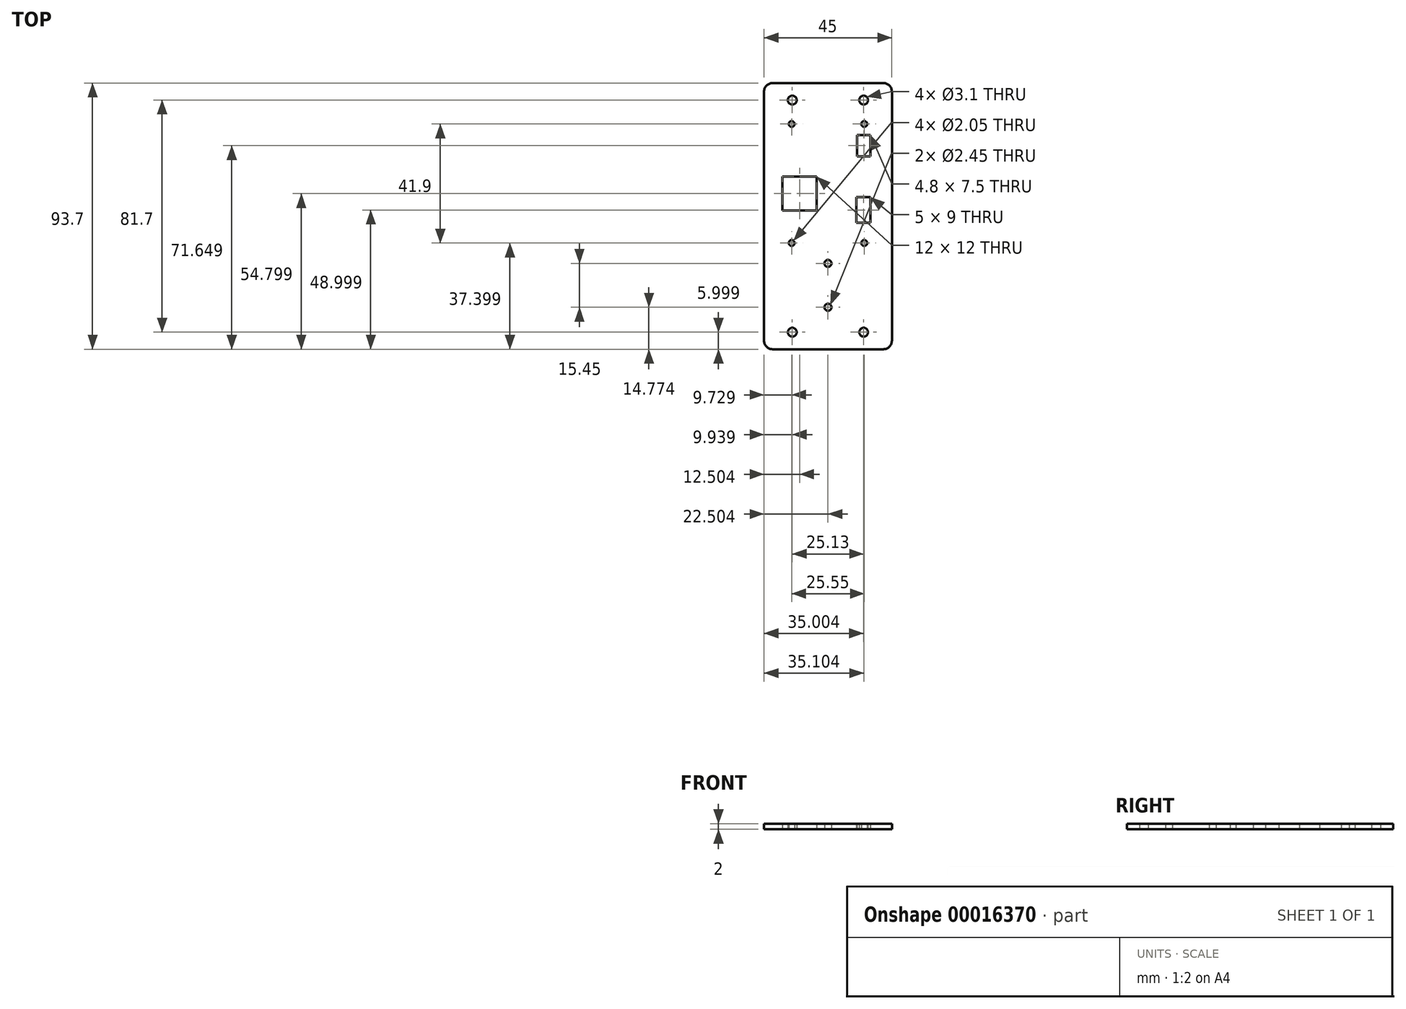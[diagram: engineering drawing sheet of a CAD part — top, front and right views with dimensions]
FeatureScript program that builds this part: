
annotation { "Feature Type Name" : "Feature", "Feature Type Description" : "" }
export const myFeature = defineFeature(function(context is Context, id is Id, definition is map)
    precondition{}
    {
        {
            var Q0;
            Q0=qCreatedBy(makeId("Top.planeOp"),FACE);
            var sketch = newSketch(context, id + "F0", { "sketchPlane" : qUnion([Q0])});
            skLineSegment(sketch, "E0.bottom", {"start": v(-24.75, 105.77) * mm, "end": v(14.25, 105.77) * mm});
            skLineSegment(sketch, "E0.top", {"start": v(-24.75, 12.07) * mm, "end": v(14.25, 12.07) * mm});
            skLineSegment(sketch, "E0.left", {"start": v(-27.75, 102.77) * mm, "end": v(-27.75, 15.07) * mm});
            skLineSegment(sketch, "E0.right", {"start": v(17.25, 102.77) * mm, "end": v(17.25, 15.07) * mm});
            skLineSegment(sketch, "E1.bottom", {"start": v(-20.25, 93.77) * mm, "end": v(9.75, 93.77) * mm});
            skLineSegment(sketch, "E1.top", {"start": v(-20.25, 47.07) * mm, "end": v(9.75, 47.07) * mm});
            skLineSegment(sketch, "E1.left", {"start": v(-20.25, 93.77) * mm, "end": v(-20.25, 47.07) * mm});
            skLineSegment(sketch, "E1.right", {"start": v(9.75, 93.77) * mm, "end": v(9.75, 47.07) * mm});
            skPoint(sketch, "E2", {"position": v(-5.25, 105.77) * mm});
            skPoint(sketch, "E3", {"position": v(-5.25, 93.77) * mm});
            skLineSegment(sketch, "E4.bottom", {"start": v(-20.25, 103.77) * mm, "end": v(9.75, 103.77) * mm});
            skLineSegment(sketch, "E4.top", {"start": v(-20.25, 95.77) * mm, "end": v(9.75, 95.77) * mm});
            skLineSegment(sketch, "E4.left", {"start": v(-20.25, 103.77) * mm, "end": v(-20.25, 95.77) * mm});
            skLineSegment(sketch, "E4.right", {"start": v(9.75, 103.77) * mm, "end": v(9.75, 95.77) * mm});
            skPoint(sketch, "E5", {"position": v(-5.25, 103.77) * mm});
            skCircle(sketch, "E6", {"center": v(-17.81, 99.77) * mm, "radius": 1.55 * mm});
            skCircle(sketch, "E7", {"center": v(7.32, 99.77) * mm, "radius": 1.55 * mm});
            skPoint(sketch, "E8", {"position": v(9.75, 99.77) * mm});
            skCircle(sketch, "E9", {"center": v(-18.02, 91.37) * mm, "radius": 1.02 * mm});
            skCircle(sketch, "E10", {"center": v(7.53, 91.37) * mm, "radius": 1.02 * mm});
            skCircle(sketch, "E11", {"center": v(-18.02, 49.47) * mm, "radius": 1.02 * mm});
            skCircle(sketch, "E12", {"center": v(7.53, 49.47) * mm, "radius": 1.02 * mm});
            skLineSegment(sketch, "E13.bottom", {"start": v(-21.25, 72.87) * mm, "end": v(-9.25, 72.87) * mm});
            skLineSegment(sketch, "E13.top", {"start": v(-21.25, 60.87) * mm, "end": v(-9.25, 60.87) * mm});
            skLineSegment(sketch, "E13.left", {"start": v(-21.25, 72.87) * mm, "end": v(-21.25, 60.87) * mm});
            skLineSegment(sketch, "E13.right", {"start": v(-9.25, 72.87) * mm, "end": v(-9.25, 60.87) * mm});
            skPoint(sketch, "E14.visualSharp", {"position": v(-21.25, 72.87) * mm});
            skPoint(sketch, "E15.visualSharp", {"position": v(-9.25, 72.87) * mm});
            skPoint(sketch, "E16.visualSharp", {"position": v(-9.25, 60.87) * mm});
            skPoint(sketch, "E17.visualSharp", {"position": v(-21.25, 60.87) * mm});
            skPoint(sketch, "E18.visualSharp", {"position": v(-27.75, 105.77) * mm});
            skArc(sketch, "E18.filletArc", {"start": v(-24.75, 105.77) * mm, "mid": v(-26.87, 104.9) * mm, "end": v(-27.75, 102.77) * mm});
            skPoint(sketch, "E19.visualSharp", {"position": v(17.25, 105.77) * mm});
            skArc(sketch, "E19.filletArc", {"start": v(17.25, 102.77) * mm, "mid": v(16.38, 104.9) * mm, "end": v(14.25, 105.77) * mm});
            skPoint(sketch, "E20.visualSharp", {"position": v(17.25, 12.07) * mm});
            skArc(sketch, "E20.filletArc", {"start": v(14.25, 12.07) * mm, "mid": v(16.38, 12.95) * mm, "end": v(17.25, 15.07) * mm});
            skPoint(sketch, "E21.visualSharp", {"position": v(-27.75, 12.07) * mm});
            skArc(sketch, "E21.filletArc", {"start": v(-27.75, 15.07) * mm, "mid": v(-26.87, 12.95) * mm, "end": v(-24.75, 12.07) * mm});
            skLineSegment(sketch, "E22.bottom", {"start": v(9.75, 87.47) * mm, "end": v(4.95, 87.47) * mm});
            skLineSegment(sketch, "E22.top", {"start": v(9.75, 79.97) * mm, "end": v(4.95, 79.97) * mm});
            skLineSegment(sketch, "E22.left", {"start": v(9.75, 87.47) * mm, "end": v(9.75, 79.97) * mm});
            skLineSegment(sketch, "E22.right", {"start": v(4.95, 87.47) * mm, "end": v(4.95, 79.97) * mm});
            skPoint(sketch, "E23", {"position": v(-5.25, 22.07) * mm});
            skCircle(sketch, "E24", {"center": v(7.32, 18.07) * mm, "radius": 1.55 * mm});
            skLineSegment(sketch, "E25.bottom", {"start": v(-20.25, 22.07) * mm, "end": v(9.75, 22.07) * mm});
            skLineSegment(sketch, "E25.top", {"start": v(-20.25, 14.07) * mm, "end": v(9.75, 14.07) * mm});
            skLineSegment(sketch, "E25.left", {"start": v(-20.25, 22.07) * mm, "end": v(-20.25, 14.07) * mm});
            skCircle(sketch, "E26", {"center": v(-17.81, 18.07) * mm, "radius": 1.55 * mm});
            skLineSegment(sketch, "E25.right", {"start": v(9.75, 22.07) * mm, "end": v(9.75, 14.07) * mm});
            skPoint(sketch, "E27", {"position": v(9.75, 18.07) * mm});
            skLineSegment(sketch, "E28.bottom", {"start": v(-10.2, 45.07) * mm, "end": v(-0.3, 45.07) * mm});
            skLineSegment(sketch, "E28.top", {"start": v(-10.2, 24.07) * mm, "end": v(-0.3, 24.07) * mm});
            skLineSegment(sketch, "E28.left", {"start": v(-10.2, 45.07) * mm, "end": v(-10.2, 24.07) * mm});
            skLineSegment(sketch, "E28.right", {"start": v(-0.3, 45.07) * mm, "end": v(-0.3, 24.07) * mm});
            skCircle(sketch, "E29", {"center": v(-5.25, 42.3) * mm, "radius": 1.23 * mm});
            skCircle(sketch, "E30", {"center": v(-5.25, 26.84) * mm, "radius": 1.23 * mm});
            skPoint(sketch, "E31", {"position": v(-5.25, 45.07) * mm});
            skLineSegment(sketch, "E32.bottom", {"start": v(9.75, 56.57) * mm, "end": v(4.75, 56.57) * mm});
            skLineSegment(sketch, "E32.top", {"start": v(9.75, 65.57) * mm, "end": v(4.75, 65.57) * mm});
            skLineSegment(sketch, "E32.left", {"start": v(9.75, 56.57) * mm, "end": v(9.75, 65.57) * mm});
            skLineSegment(sketch, "E32.right", {"start": v(4.75, 56.57) * mm, "end": v(4.75, 65.57) * mm});
            skPoint(sketch, "E33", {"position": v(-5.25, 12.07) * mm});
            skPoint(sketch, "E34", {"position": v(-5.25, 24.07) * mm});
            skSolve(sketch);
        }
        {
            var Q0;
            Q0 = qSketchRegion(id + "F0", true);
            var Q1;
            {var subQ7=sQuery(id+"F0.wireOp",EDGE,"E1.bottom");Q1=makeQuery(id+"F0.imprint","IMPRINT",FACE,{"disambiguationData":[TD([[makeQuery(id+"F0.imprint","IMPRINT",EDGE,{"derivedFrom":subQ7}),-1.0]])]});}
            var Q2;
            Q2=makeQuery(id+"F0.imprint","IMPRINT",FACE,{"disambiguationData":[TD([[makeQuery(id+"F0.imprint","IMPRINT",EDGE,{"derivedFrom":sQuery(id+"F0.wireOp",EDGE,"E4.bottom")}),-1.0]])]});
            var Q3;
            Q3=makeQuery(id+"F0.imprint","IMPRINT",FACE,{"disambiguationData":[TD([[makeQuery(id+"F0.imprint","IMPRINT",EDGE,{"derivedFrom":sQuery(id+"F0.wireOp",EDGE,"E28.bottom")}),-1.0]])]});
            var Q4;
            Q4=makeQuery(id+"F0.imprint","IMPRINT",FACE,{"disambiguationData":[TD([[makeQuery(id+"F0.imprint","IMPRINT",EDGE,{"derivedFrom":sQuery(id+"F0.wireOp",EDGE,"E24")}),-1.0]])]});
            extrude(context, id + "F1", {"entities" : qUnion([Q0, Q1, Q2, Q3, Q4]), "depth" : 2 * mm});
        }
    });
